# Revit family: Accessory-Shower_Shelf-KOHLER-CHOREOGRAPH-K-97623_1
name_source: partatom
category: Specialty Equipment
revit_build: Autodesk Revit 2017 (Build: 20160225_1515(x64)
units: mm (PartAtom-declared; Revit-internal decimal feet)

## family parameters
Cut with Voids When Loaded = No
Host = Face
OmniClass Number = 23.31.25.00
OmniClass Title = Toilet and Bath Specialties
Part Type = Normal
Room Calculation Point = No
Round Connector Dimension = Use Diameter
Shared = No

## types (4) — shared parameters
ADA Compliant = No
Assembly Code = C1030200
Date Modified = 09/17/2021
Default Elevation = 42"
Description = 21 Inch floating shower shelf
Height = 2"
Length = 3 3/8"
Manufacturer = KOHLER Co.
Master Format 2014 = 10 28 00
Master Format 2014 Name = Toilet, Bath, and Laundry Accessories
Material = Anodized Aluminium
Product Documentation Link = https://www.us.kohler.com
Product Name = CHOREOGRAPH
Product Page URL = https://www.us.kohler.com
URL = https://www.us.kohler.com
WaterSense Certified = No
Width = 21"

## per-type parameters (varying)
| type | Finish | Model | Type |
| SHP-Bright Polished Silver | Kohler-Metal-SHP-Bright_Polished_Silver | K-97623-SHP | 1 |
| BNK-Anodized Brushed Nickel | Kohler-Metal-BNK-Anodized_Brushed_Nickel | K-97623-BNK | 2 |
| ABZ-Anodized Dark Bronze | Kohler-Metal-ABZ-Anodized_Dark_Bronze | K-97623-ABZ | 3 |
| BL-Matte Black | Kohler-Metal-BL-Matte_Black | K-97623-BL | 4 |

## geometry (parser evidence)
native form markers: Sweep x4
no freeform markers — native parametric forms only
